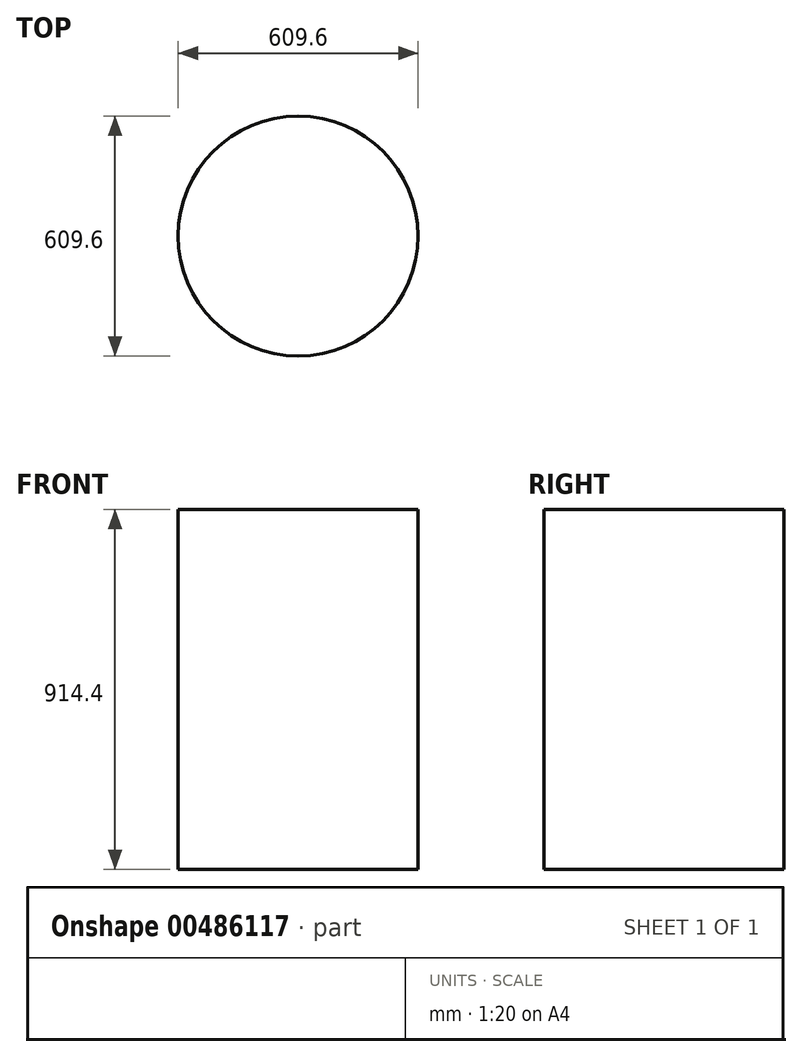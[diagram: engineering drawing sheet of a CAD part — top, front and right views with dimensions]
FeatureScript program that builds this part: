
annotation { "Feature Type Name" : "Feature", "Feature Type Description" : "" }
export const myFeature = defineFeature(function(context is Context, id is Id, definition is map)
    precondition{}
    {
        {
            var Q0;
            Q0=qCreatedBy(makeId("Top.planeOp"),FACE);
            var sketch = newSketch(context, id + "F0", { "sketchPlane" : qUnion([Q0])});
            skCircle(sketch, "E0", {"center": v(0, 0) * mm, "radius": 304.8 * mm});
            skSolve(sketch);
        }
        {
            var Q0;
            Q0 = qSketchRegion(id + "F0", true);
            extrude(context, id + "F1", {"entities" : qUnion([Q0]), "depth" : 914.4 * mm});
        }
    });
